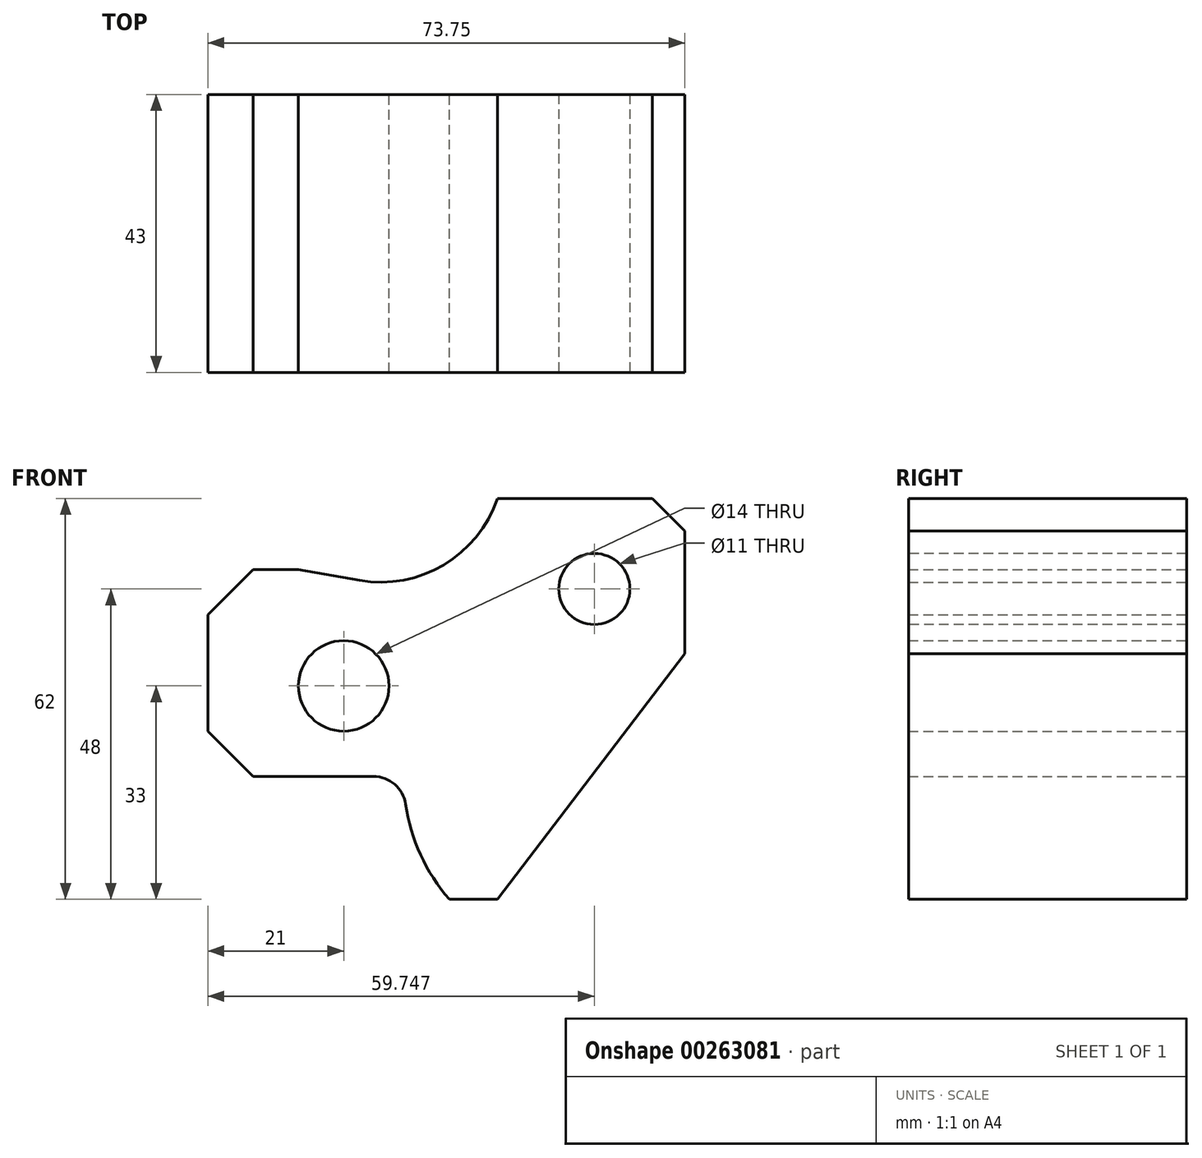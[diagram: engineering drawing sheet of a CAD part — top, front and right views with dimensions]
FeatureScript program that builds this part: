
annotation { "Feature Type Name" : "Feature", "Feature Type Description" : "" }
export const myFeature = defineFeature(function(context is Context, id is Id, definition is map)
    precondition{}
    {
        {
            var Q0;
            Q0=qCreatedBy(makeId("Front.planeOp"),FACE);
            var sketch = newSketch(context, id + "F0", { "sketchPlane" : qUnion([Q0])});
            skCircle(sketch, "E0", {"center": v(0, 0) * mm, "radius": 7 * mm});
            skLineSegment(sketch, "E1", {"start": v(-21, 11) * mm, "end": v(-21, -7) * mm});
            skLineSegment(sketch, "E2", {"start": v(-21, -7) * mm, "end": v(-14, -14) * mm});
            skLineSegment(sketch, "E3", {"start": v(-21, -7) * mm, "end": v(-21, -65.16) * mm, "construction": true});
            skLineSegment(sketch, "E4", {"start": v(-21, 11) * mm, "end": v(-14, 18) * mm});
            skLineSegment(sketch, "E5", {"start": v(-21, 11) * mm, "end": v(-21, 49.66) * mm, "construction": true});
            skLineSegment(sketch, "E6", {"start": v(0, 0) * mm, "end": v(-37.47, 0) * mm, "construction": true});
            skLineSegment(sketch, "E7", {"start": v(-14, 18) * mm, "end": v(-7, 18) * mm});
            skLineSegment(sketch, "E8", {"start": v(52.75, 24) * mm, "end": v(52.75, 5) * mm});
            skLineSegment(sketch, "E9", {"start": v(52.75, 24) * mm, "end": v(47.75, 29) * mm});
            skLineSegment(sketch, "E10", {"start": v(52.75, 24) * mm, "end": v(52.75, 46.8) * mm, "construction": true});
            skLineSegment(sketch, "E11", {"start": v(16.34, -33) * mm, "end": v(23.75, -33) * mm});
            skLineSegment(sketch, "E12", {"start": v(47.75, 29) * mm, "end": v(23.75, 29) * mm});
            skLineSegment(sketch, "E13", {"start": v(23.75, -33) * mm, "end": v(52.75, 5) * mm});
            skPoint(sketch, "E14.endSnap0", {"position": v(38.25, -14) * mm});
            skLineSegment(sketch, "E15", {"start": v(-7, 18) * mm, "end": v(2.44, 16.34) * mm});
            skLineSegment(sketch, "E16", {"start": v(-7, 18) * mm, "end": v(13.5, 18) * mm, "construction": true});
            skArc(sketch, "E17", {"start": v(2.44, 16.34) * mm, "mid": v(15.44, 18.71) * mm, "end": v(23.75, 29) * mm});
            skArc(sketch, "E18", {"start": v(16.34, -33) * mm, "mid": v(11.9, -26.12) * mm, "end": v(9.56, -18.26) * mm});
            skLineSegment(sketch, "E19", {"start": v(-14, -14) * mm, "end": v(4.62, -14) * mm});
            skPoint(sketch, "E20.visualSharp", {"position": v(9.25, -14) * mm});
            skArc(sketch, "E20.filletArc", {"start": v(9.56, -18.26) * mm, "mid": v(7.88, -15.21) * mm, "end": v(4.62, -14) * mm});
            skSolve(sketch);
        }
        {
            var Q0;
            Q0 = qSketchRegion(id + "F0", true);
            extrude(context, id + "F1", {"entities" : qUnion([Q0]), "depth" : 43 * mm});
        }
        {
            var Q0;
            Q0=makeQuery(id+"F1.opExtrude","CAP_FACE",FACE,{"disambiguationData":[OSD([sQuery(id+"F0.wireOp",EDGE,"E0"),sQuery(id+"F0.wireOp",EDGE,"E1"),sQuery(id+"F0.wireOp",EDGE,"E2"),sQuery(id+"F0.wireOp",EDGE,"E4"),sQuery(id+"F0.wireOp",EDGE,"E7"),sQuery(id+"F0.wireOp",EDGE,"E8"),sQuery(id+"F0.wireOp",EDGE,"E9"),sQuery(id+"F0.wireOp",EDGE,"E11"),sQuery(id+"F0.wireOp",EDGE,"E12"),sQuery(id+"F0.wireOp",EDGE,"E13"),sQuery(id+"F0.wireOp",EDGE,"E15"),sQuery(id+"F0.wireOp",EDGE,"E17"),sQuery(id+"F0.wireOp",EDGE,"E18"),sQuery(id+"F0.wireOp",EDGE,"E19"),sQuery(id+"F0.wireOp",EDGE,"E20.filletArc")])],"isStart":false});
            var sketch = newSketch(context, id + "F2", { "sketchPlane" : qUnion([Q0])});
            skCircle(sketch, "E21", {"center": v(38.75, 15) * mm, "radius": 5.5 * mm});
            skSolve(sketch);
        }
        {
            var Q0;
            Q0 = qSketchRegion(id + "F2", true);
            extrude(context, id + "F3", {"entities" : qUnion([Q0]), "operationType" : NewBodyOperationType.REMOVE, "endBound" : BoundingType.THROUGH_ALL, "oppositeDirection" : true, "depth" : 25 * mm});
        }
    });
